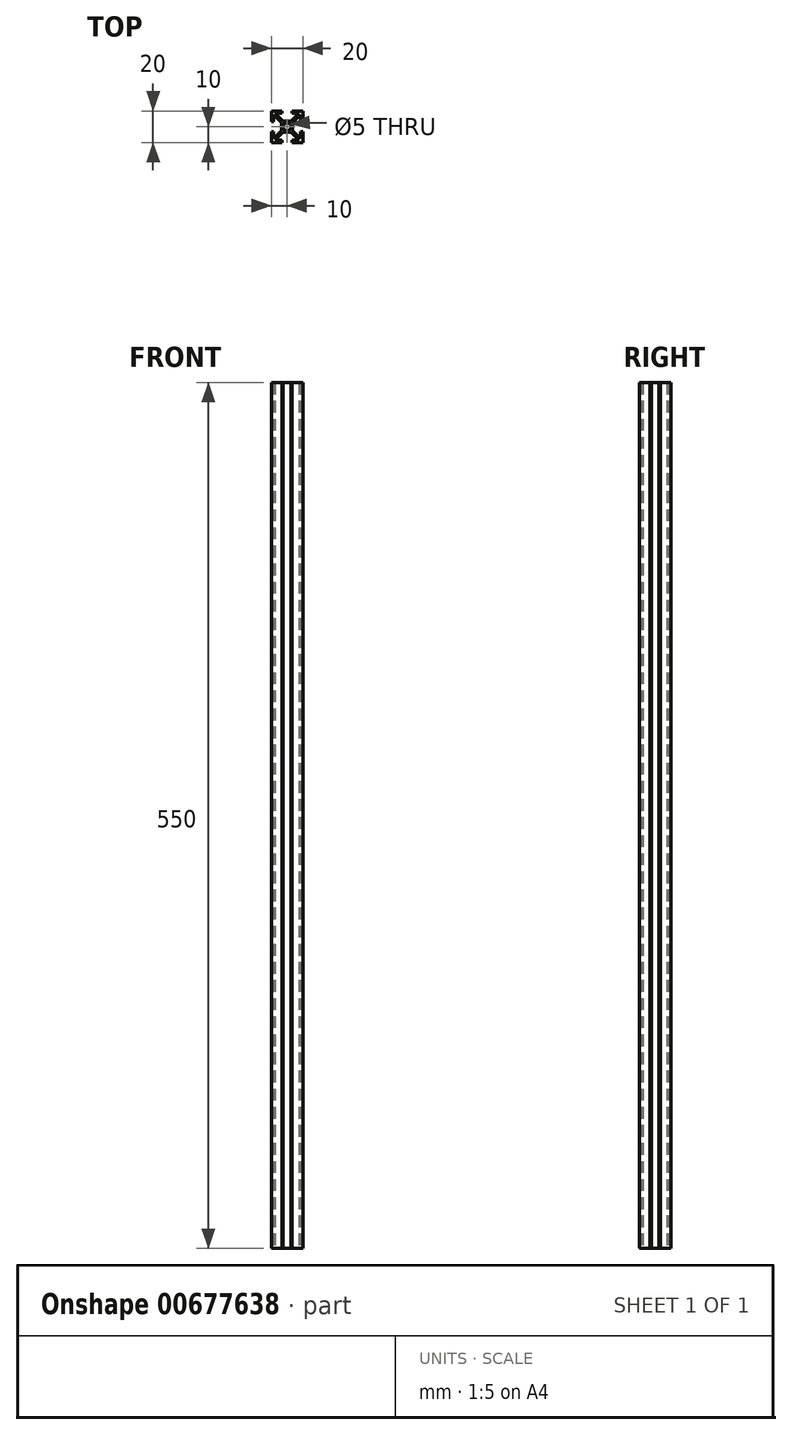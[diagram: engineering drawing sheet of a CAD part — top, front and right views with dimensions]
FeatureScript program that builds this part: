
annotation { "Feature Type Name" : "Feature", "Feature Type Description" : "" }
export const myFeature = defineFeature(function(context is Context, id is Id, definition is map)
    precondition{}
    {
        {
            var Q0;
            Q0=qCreatedBy(makeId("Top.planeOp"),FACE);
            var sketch = newSketch(context, id + "F0", { "sketchPlane" : qUnion([Q0])});
            skCircle(sketch, "E0", {"center": v(10, 10) * mm, "radius": 2.5 * mm});
            skLineSegment(sketch, "E1", {"start": v(0, 0) * mm, "end": v(10, 10) * mm, "construction": true});
            skLineSegment(sketch, "E2", {"start": v(1.4, 2.39) * mm, "end": v(1.4, 6.8) * mm});
            skLineSegment(sketch, "E3", {"start": v(1.4, 6.8) * mm, "end": v(0, 6.8) * mm});
            skLineSegment(sketch, "E4", {"start": v(0, 6.8) * mm, "end": v(0, 0) * mm});
            skLineSegment(sketch, "E5", {"start": v(7.49, 6.5) * mm, "end": v(2.39, 1.4) * mm});
            skLineSegment(sketch, "E6", {"start": v(2.39, 1.4) * mm, "end": v(6.8, 1.4) * mm});
            skLineSegment(sketch, "E7", {"start": v(6.8, 1.4) * mm, "end": v(6.8, 0) * mm});
            skLineSegment(sketch, "E8", {"start": v(6.8, 0) * mm, "end": v(0, 0) * mm});
            skLineSegment(sketch, "E9", {"start": v(10, 10) * mm, "end": v(20, 20) * mm, "construction": true});
            skLineSegment(sketch, "E10", {"start": v(10, 10) * mm, "end": v(0, 20) * mm, "construction": true});
            skLineSegment(sketch, "E11", {"start": v(10, 10) * mm, "end": v(20, 0) * mm, "construction": true});
            skLineSegment(sketch, "E12", {"start": v(1.4, 17.61) * mm, "end": v(6.5, 12.51) * mm});
            skLineSegment(sketch, "E13", {"start": v(1.4, 17.61) * mm, "end": v(1.4, 13.2) * mm});
            skLineSegment(sketch, "E14", {"start": v(1.4, 13.2) * mm, "end": v(0, 13.2) * mm});
            skLineSegment(sketch, "E15", {"start": v(0, 13.2) * mm, "end": v(0, 20) * mm});
            skLineSegment(sketch, "E16", {"start": v(7.49, 13.5) * mm, "end": v(2.39, 18.6) * mm});
            skLineSegment(sketch, "E17", {"start": v(2.39, 18.6) * mm, "end": v(6.8, 18.6) * mm});
            skLineSegment(sketch, "E18", {"start": v(6.8, 18.6) * mm, "end": v(6.8, 20) * mm});
            skLineSegment(sketch, "E19", {"start": v(6.8, 20) * mm, "end": v(0, 20) * mm});
            skLineSegment(sketch, "E20", {"start": v(12.51, 13.5) * mm, "end": v(17.61, 18.6) * mm});
            skLineSegment(sketch, "E21", {"start": v(17.61, 18.6) * mm, "end": v(13.2, 18.6) * mm});
            skLineSegment(sketch, "E22", {"start": v(13.2, 18.6) * mm, "end": v(13.2, 20) * mm});
            skLineSegment(sketch, "E23", {"start": v(13.2, 20) * mm, "end": v(20, 20) * mm});
            skLineSegment(sketch, "E24", {"start": v(13.5, 12.51) * mm, "end": v(18.6, 17.61) * mm});
            skLineSegment(sketch, "E25", {"start": v(18.6, 17.61) * mm, "end": v(18.6, 13.2) * mm});
            skLineSegment(sketch, "E26", {"start": v(18.6, 13.2) * mm, "end": v(20, 13.2) * mm});
            skLineSegment(sketch, "E27", {"start": v(20, 13.2) * mm, "end": v(20, 20) * mm});
            skLineSegment(sketch, "E28", {"start": v(18.6, 2.39) * mm, "end": v(18.6, 6.8) * mm});
            skLineSegment(sketch, "E29", {"start": v(18.6, 6.8) * mm, "end": v(20, 6.8) * mm});
            skLineSegment(sketch, "E30", {"start": v(20, 6.8) * mm, "end": v(20, 0) * mm});
            skLineSegment(sketch, "E31", {"start": v(12.51, 6.5) * mm, "end": v(17.61, 1.4) * mm});
            skLineSegment(sketch, "E32", {"start": v(17.61, 1.4) * mm, "end": v(13.2, 1.4) * mm});
            skLineSegment(sketch, "E33", {"start": v(13.2, 1.4) * mm, "end": v(13.2, 0) * mm});
            skLineSegment(sketch, "E34", {"start": v(13.2, 0) * mm, "end": v(20, 0) * mm});
            skLineSegment(sketch, "E35", {"start": v(12.51, 6.5) * mm, "end": v(7.49, 6.5) * mm});
            skLineSegment(sketch, "E36", {"start": v(7.49, 13.5) * mm, "end": v(12.51, 13.5) * mm});
            skLineSegment(sketch, "E37", {"start": v(10, 10) * mm, "end": v(10, 0) * mm, "construction": true});
            skLineSegment(sketch, "E38", {"start": v(10, 10) * mm, "end": v(18.77, 10) * mm, "construction": true});
            skLineSegment(sketch, "E39", {"start": v(10, 10) * mm, "end": v(10, 20.74) * mm, "construction": true});
            skLineSegment(sketch, "E40", {"start": v(10, 10) * mm, "end": v(0, 10) * mm, "construction": true});
            skLineSegment(sketch, "E41.bottom", {"start": v(0, 0) * mm, "end": v(20, 0) * mm, "construction": true});
            skLineSegment(sketch, "E41.top", {"start": v(0, 20) * mm, "end": v(20, 20) * mm, "construction": true});
            skLineSegment(sketch, "E41.left", {"start": v(0, 0) * mm, "end": v(0, 20) * mm, "construction": true});
            skLineSegment(sketch, "E41.right", {"start": v(20, 0) * mm, "end": v(20, 20) * mm, "construction": true});
            skLineSegment(sketch, "E42", {"start": v(18.6, 2.39) * mm, "end": v(13.5, 7.49) * mm});
            skLineSegment(sketch, "E43", {"start": v(13.5, 7.49) * mm, "end": v(13.5, 12.51) * mm});
            skLineSegment(sketch, "E44", {"start": v(1.4, 2.39) * mm, "end": v(6.5, 7.62) * mm});
            skLineSegment(sketch, "E45", {"start": v(6.5, 7.62) * mm, "end": v(6.5, 12.51) * mm});
            skSolve(sketch);
        }
        {
            var Q0;
            Q0=makeQuery(id+"F0.imprint","IMPRINT",FACE,{"disambiguationData":[TD([[makeQuery(id+"F0.imprint","IMPRINT",EDGE,{"derivedFrom":sQuery(id+"F0.wireOp",EDGE,"E0")}),-1.0]])]});
            extrude(context, id + "F1", {"entities" : qUnion([Q0]), "depth" : 550 * mm, "offsetDistance" : 25 * mm});
        }
    });
